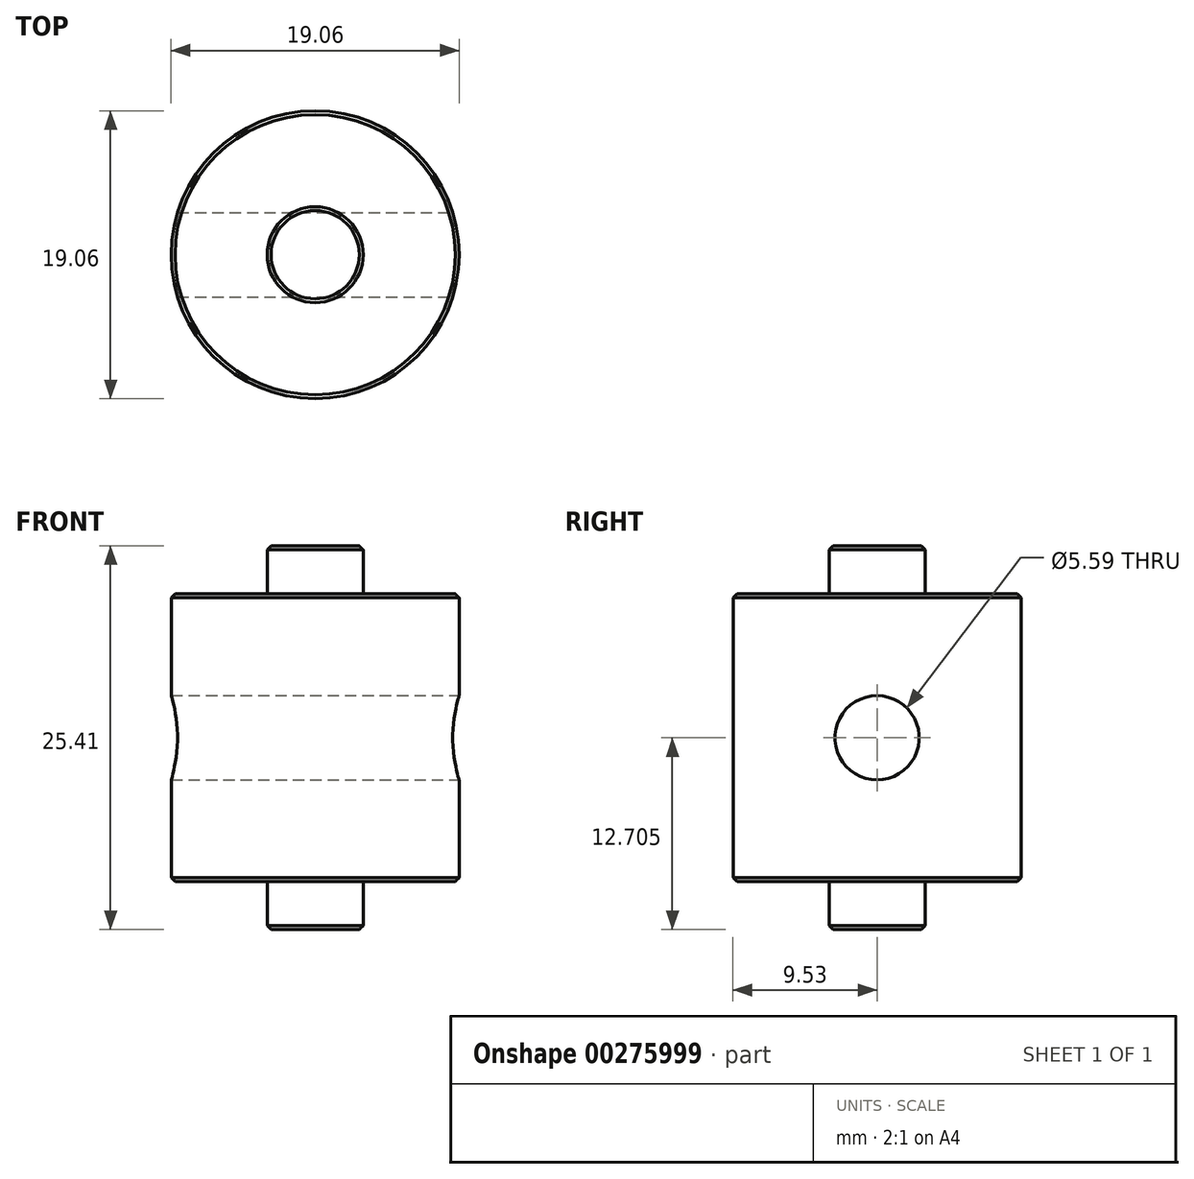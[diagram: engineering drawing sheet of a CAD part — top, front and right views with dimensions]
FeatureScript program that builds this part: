
annotation { "Feature Type Name" : "Feature", "Feature Type Description" : "" }
export const myFeature = defineFeature(function(context is Context, id is Id, definition is map)
    precondition{}
    {
        {
            var Q0;
            Q0=qCreatedBy(makeId("Top.planeOp"),FACE);
            var sketch = newSketch(context, id + "F0", { "sketchPlane" : qUnion([Q0])});
            skCircle(sketch, "E0", {"center": v(0, 0) * mm, "radius": 9.53 * mm});
            skSolve(sketch);
        }
        {
            var Q0;
            Q0=qSketchRegion(id+"F0",true);
            extrude(context, id + "F1", {"entities" : qUnion([Q0]), "depth" : 19.05 * mm});
        }
        {
            var Q0;
            Q0=qCreatedBy(makeId("Top.planeOp"),FACE);
            var sketch = newSketch(context, id + "F2", { "sketchPlane" : qUnion([Q0])});
            skCircle(sketch, "E1", {"center": v(0, 0) * mm, "radius": 3.18 * mm});
            skSolve(sketch);
        }
        {
            var Q0;
            Q0=qSketchRegion(id+"F2",true);
            extrude(context, id + "F3", {"entities" : qUnion([Q0]), "operationType" : NewBodyOperationType.ADD, "oppositeDirection" : true, "depth" : 3.17 * mm});
        }
        {
            var Q0;
            Q0=makeQuery(id+"F1.opExtrude","CAP_FACE",FACE,{"disambiguationData":[OSD([sQuery(id+"F0.wireOp",EDGE,"E0")])],"isStart":false});
            var sketch = newSketch(context, id + "F4", { "sketchPlane" : qUnion([Q0])});
            skCircle(sketch, "E2", {"center": v(0, 0) * mm, "radius": 3.18 * mm});
            skSolve(sketch);
        }
        {
            var Q0;
            Q0=qSketchRegion(id+"F4",true);
            extrude(context, id + "F5", {"entities" : qUnion([Q0]), "operationType" : NewBodyOperationType.ADD, "depth" : 3.17 * mm});
        }
        {
            var Q0;
            Q0=makeQuery(id+"F5.opExtrude","CAP_EDGE",EDGE,{"disambiguationData":[OSD([sQuery(id+"F4.wireOp",EDGE,"E2")])],"isStart":false});
            var Q1;
            Q1=makeQuery(id+"F1.opExtrude","CAP_EDGE",EDGE,{"disambiguationData":[OSD([sQuery(id+"F0.wireOp",EDGE,"E0")])],"isStart":false});
            var Q2;
            Q2=makeQuery(id+"F3.opExtrude","CAP_EDGE",EDGE,{"disambiguationData":[OSD([sQuery(id+"F2.wireOp",EDGE,"E1")])],"isStart":false});
            var Q3;
            Q3=makeQuery(id+"F1.opExtrude","CAP_EDGE",EDGE,{"disambiguationData":[OSD([sQuery(id+"F0.wireOp",EDGE,"E0")])],"isStart":true});
            chamfer(context, id + "F6", {"entities" : qUnion([Q0, Q1, Q2, Q3]), "width" : 0.25 * mm, "tangentPropagation" : true});
        }
        {
            var Q0;
            Q0=qCreatedBy(makeId("Right.planeOp"),FACE);
            var sketch = newSketch(context, id + "F7", { "sketchPlane" : qUnion([Q0])});
            skCircle(sketch, "E3", {"center": v(0, 9.53) * mm, "radius": 2.8 * mm});
            skSolve(sketch);
        }
        {
            var Q0;
            Q0 = qSketchRegion(id + "F7", true);
            extrude(context, id + "F8", {"entities" : qUnion([Q0]), "operationType" : NewBodyOperationType.REMOVE, "oppositeDirection" : true, "depth" : 25.4 * mm});
        }
        {
            var Q0;
            Q0 = qSketchRegion(id + "F7", true);
            extrude(context, id + "F9", {"entities" : qUnion([Q0]), "operationType" : NewBodyOperationType.REMOVE, "depth" : 25.4 * mm});
        }
    });
